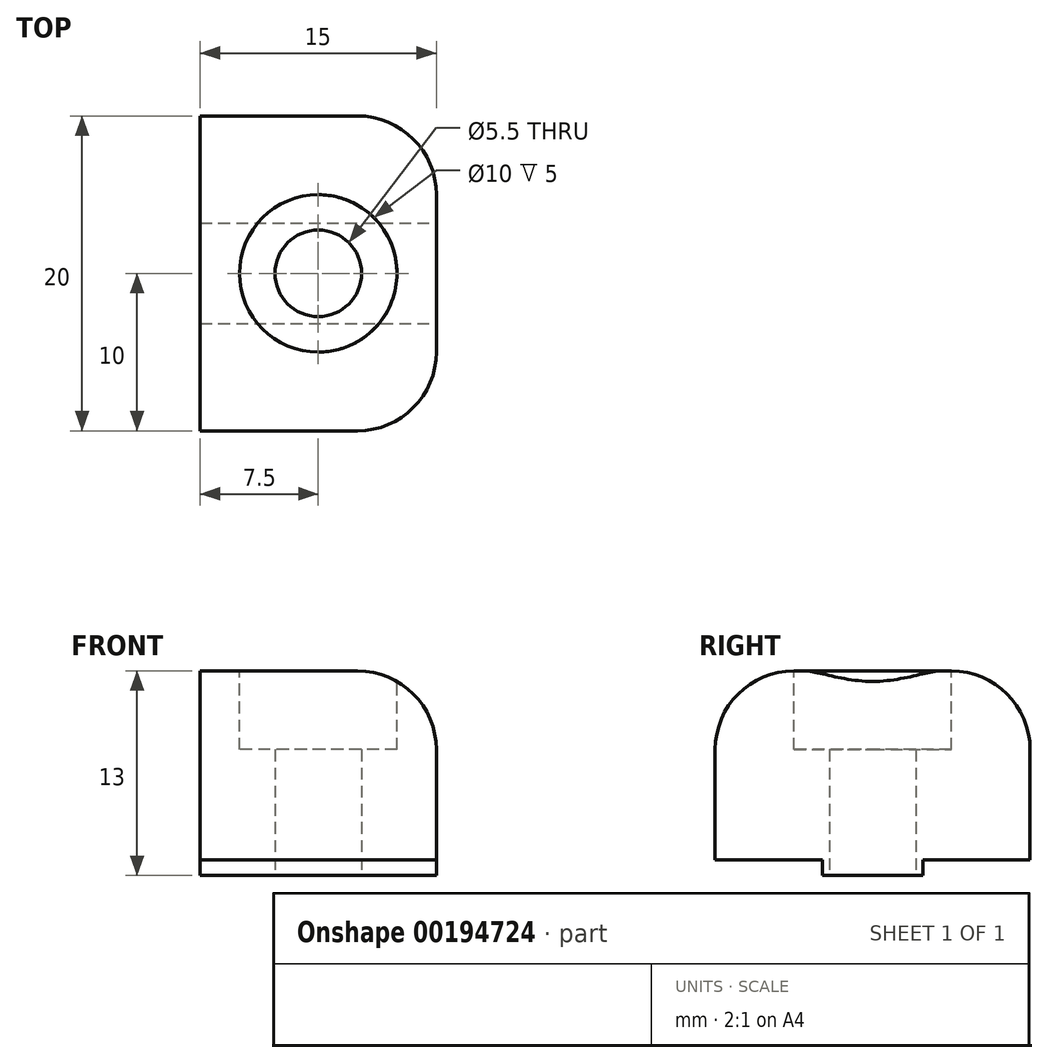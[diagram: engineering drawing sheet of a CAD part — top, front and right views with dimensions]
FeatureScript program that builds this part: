
annotation { "Feature Type Name" : "Feature", "Feature Type Description" : "" }
export const myFeature = defineFeature(function(context is Context, id is Id, definition is map)
    precondition{}
    {
        {
            var Q0;
            Q0=qCreatedBy(makeId("Top.planeOp"),FACE);
            var sketch = newSketch(context, id + "F0", { "sketchPlane" : qUnion([Q0])});
            skLineSegment(sketch, "E0.bottom", {"start": v(7.5, 10) * mm, "end": v(-7.5, 10) * mm});
            skLineSegment(sketch, "E0.top", {"start": v(7.5, -10) * mm, "end": v(-7.5, -10) * mm});
            skLineSegment(sketch, "E0.left", {"start": v(7.5, 10) * mm, "end": v(7.5, -10) * mm});
            skLineSegment(sketch, "E0.right", {"start": v(-7.5, 10) * mm, "end": v(-7.5, -10) * mm});
            skPoint(sketch, "E0.middle", {"position": v(0, 0) * mm});
            skCircle(sketch, "E1", {"center": v(0, 0) * mm, "radius": 2.75 * mm});
            skSolve(sketch);
        }
        {
            var Q0;
            Q0 = qSketchRegion(id + "F0", true);
            extrude(context, id + "F1", {"entities" : qUnion([Q0]), "depth" : 12 * mm});
        }
        {
            var Q0;
            Q0=makeQuery(id+"F1.opExtrude","CAP_FACE",FACE,{"disambiguationData":[OSD([sQuery(id+"F0.wireOp",EDGE,"E0.bottom"),sQuery(id+"F0.wireOp",EDGE,"E0.top"),sQuery(id+"F0.wireOp",EDGE,"E0.left"),sQuery(id+"F0.wireOp",EDGE,"E0.right"),sQuery(id+"F0.wireOp",EDGE,"E1")])],"isStart":false});
            var sketch = newSketch(context, id + "F2", { "sketchPlane" : qUnion([Q0])});
            skCircle(sketch, "E2", {"center": v(0, 0) * mm, "radius": 5 * mm});
            skSolve(sketch);
        }
        {
            var Q0;
            Q0=makeQuery(id+"F2.imprint","IMPRINT",FACE,{"disambiguationData":[TD([[makeQuery(id+"F2.imprint","IMPRINT",EDGE,{"derivedFrom":sQuery(id+"F2.wireOp",EDGE,"E2")}),1.0]])]});
            extrude(context, id + "F3", {"entities" : qUnion([Q0]), "operationType" : NewBodyOperationType.REMOVE, "oppositeDirection" : true, "depth" : 5 * mm});
        }
        {
            var Q0;
            Q0=makeQuery(id+"F1.opExtrude","CAP_EDGE",EDGE,{"disambiguationData":[OSD([sQuery(id+"F0.wireOp",EDGE,"E0.top")])],"isStart":false});
            var Q1;
            Q1=makeQuery(id+"F1.opExtrude","CAP_EDGE",EDGE,{"disambiguationData":[OSD([sQuery(id+"F0.wireOp",EDGE,"E0.bottom")])],"isStart":false});
            var Q2;
            Q2=makeQuery(id+"F1.opExtrude","CAP_EDGE",EDGE,{"disambiguationData":[OSD([sQuery(id+"F0.wireOp",EDGE,"E0.left")])],"isStart":false});
            fillet(context, id + "F4", {"entities" : qUnion([Q0, Q1, Q2]), "radius" : 5 * mm, "tangentPropagation" : true, "allowEdgeOverflow" : false});
        }
        {
            var Q0;
            Q0=makeQuery(id+"F1.opExtrude","SWEPT_EDGE",EDGE,{"disambiguationData":[OSD([sQuery(id+"F0.wireOp",EDGE,"E0.top"),sQuery(id+"F0.wireOp",EDGE,"E0.left")])]});
            var Q1;
            Q1=makeQuery(id+"F1.opExtrude","SWEPT_EDGE",EDGE,{"disambiguationData":[OSD([sQuery(id+"F0.wireOp",EDGE,"E0.bottom"),sQuery(id+"F0.wireOp",EDGE,"E0.left")])]});
            fillet(context, id + "F5", {"entities" : qUnion([Q0, Q1]), "radius" : 5 * mm, "tangentPropagation" : true, "allowEdgeOverflow" : false});
        }
        {
            var Q0;
            Q0=makeQuery(id+"F1.opExtrude","CAP_FACE",FACE,{"disambiguationData":[OSD([sQuery(id+"F0.wireOp",EDGE,"E0.bottom"),sQuery(id+"F0.wireOp",EDGE,"E0.top"),sQuery(id+"F0.wireOp",EDGE,"E0.left"),sQuery(id+"F0.wireOp",EDGE,"E0.right"),sQuery(id+"F0.wireOp",EDGE,"E1")])],"isStart":true});
            var sketch = newSketch(context, id + "F6", { "sketchPlane" : qUnion([Q0])});
            skPoint(sketch, "E3.middle", {"position": v(0, 0) * mm});
            skLineSegment(sketch, "E4", {"start": v(-7.5, 10) * mm, "end": v(-7.5, 3.2) * mm, "construction": true});
            skLineSegment(sketch, "E5", {"start": v(-7.5, 3.2) * mm, "end": v(7.5, 3.2) * mm});
            skLineSegment(sketch, "E6", {"start": v(-7.5, -10) * mm, "end": v(-7.5, -3.2) * mm, "construction": true});
            skLineSegment(sketch, "E7", {"start": v(-7.5, -3.2) * mm, "end": v(7.5, -3.2) * mm});
            skLineSegment(sketch, "E8", {"start": v(7.5, -3.2) * mm, "end": v(7.5, 3.2) * mm});
            skLineSegment(sketch, "E9", {"start": v(-7.5, -3.2) * mm, "end": v(-7.5, 3.2) * mm});
            skSolve(sketch);
        }
        {
            var Q0;
            Q0=makeQuery(id+"F6.imprint","IMPRINT",FACE,{"disambiguationData":[TD([[makeQuery(id+"F6.imprint","IMPRINT",EDGE,{"derivedFrom":sQuery(id+"F6.wireOp",EDGE,"E5")}),-1.0]])]});
            extrude(context, id + "F7", {"entities" : qUnion([Q0]), "operationType" : NewBodyOperationType.ADD, "depth" : 1 * mm});
        }
    });
